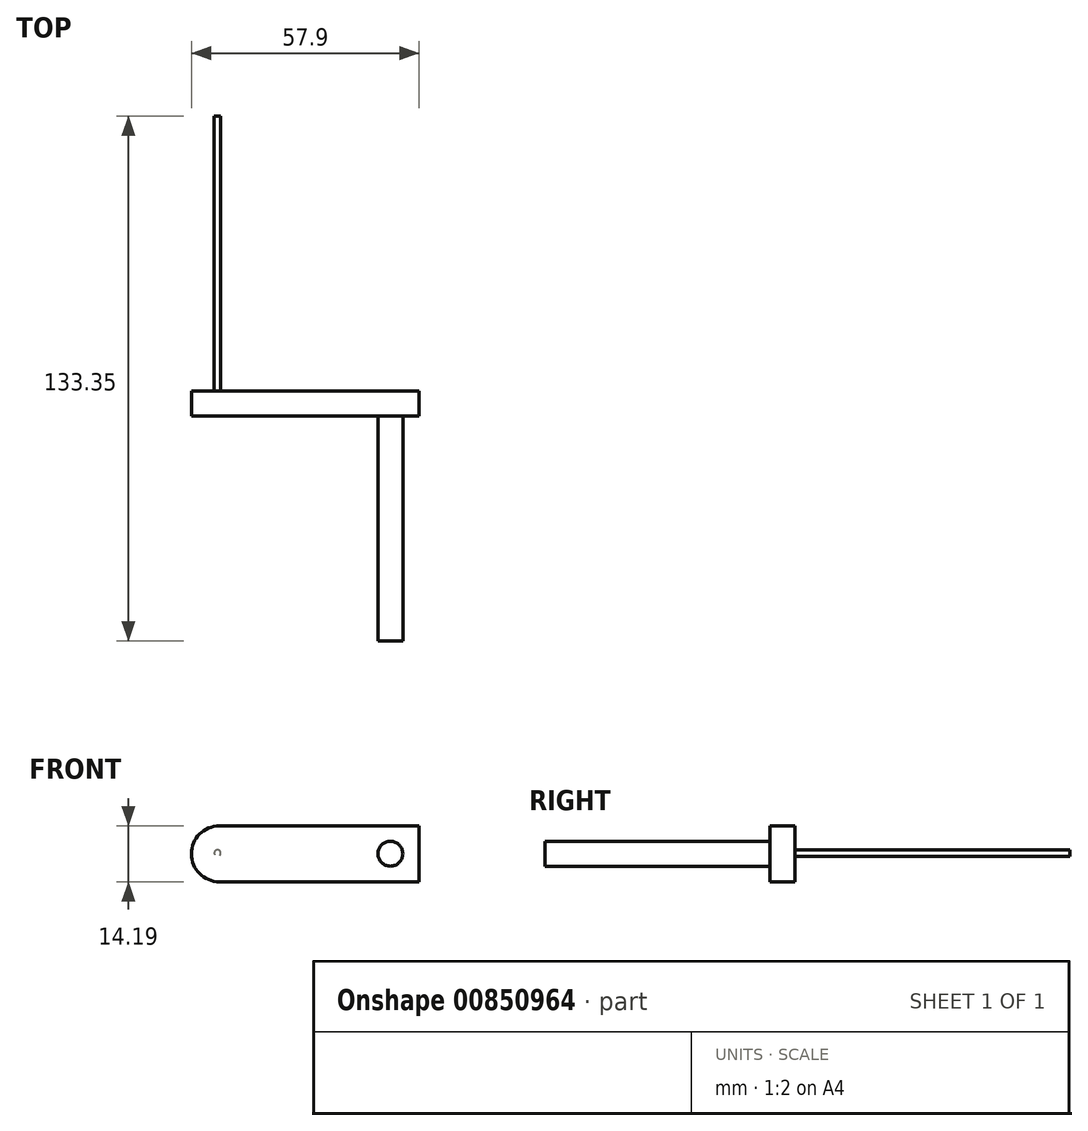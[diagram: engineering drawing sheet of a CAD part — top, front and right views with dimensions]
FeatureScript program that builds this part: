
annotation { "Feature Type Name" : "Feature", "Feature Type Description" : "" }
export const myFeature = defineFeature(function(context is Context, id is Id, definition is map)
    precondition{}
    {
        {
            var Q0;
            Q0=qCreatedBy(makeId("Front.planeOp"),FACE);
            var sketch = newSketch(context, id + "F0", { "sketchPlane" : qUnion([Q0])});
            skLineSegment(sketch, "E0.bottom", {"start": v(-42.12, 21.25) * mm, "end": v(8.68, 21.25) * mm});
            skLineSegment(sketch, "E0.top", {"start": v(-42.12, 7.06) * mm, "end": v(8.68, 7.06) * mm});
            skLineSegment(sketch, "E0.right", {"start": v(8.68, 21.25) * mm, "end": v(8.68, 7.06) * mm});
            skArc(sketch, "E1", {"start": v(-42.12, 21.25) * mm, "mid": v(-49.22, 14.15) * mm, "end": v(-42.12, 7.06) * mm});
            skPoint(sketch, "E2", {"position": v(-42.12, 21.25) * mm});
            skPoint(sketch, "E3", {"position": v(-42.12, 7.06) * mm});
            skSolve(sketch);
        }
        {
            var Q0;
            Q0=makeQuery(id+"F0.imprint","IMPRINT",FACE,{"disambiguationData":[TD([[makeQuery(id+"F0.imprint","IMPRINT",EDGE,{"derivedFrom":sQuery(id+"F0.wireOp",EDGE,"E0.bottom")}),-1.0]])]});
            extrude(context, id + "F1", {"entities" : qUnion([Q0]), "depth" : 6.35 * mm, "offsetDistance" : 25.4 * mm});
        }
        {
            var Q0;
            Q0=makeQuery(id+"F1.opExtrude","CAP_FACE",FACE,{"disambiguationData":[OSD([sQuery(id+"F0.wireOp",EDGE,"E0.bottom"),sQuery(id+"F0.wireOp",EDGE,"E0.top"),sQuery(id+"F0.wireOp",EDGE,"E0.right"),sQuery(id+"F0.wireOp",EDGE,"E1"),sQuery(id+"F0.wireOp",EDGE,"cYWnUQRV-fGSr-Q5LM-tKaJ-2oR27xkRg5be")])],"isStart":false});
            var sketch = newSketch(context, id + "F2", { "sketchPlane" : qUnion([Q0])});
            skSolve(sketch);
        }
        {
            var Q0;
            Q0=makeQuery(id+"F2.imprint","IMPRINT",FACE,{"disambiguationData":[TD([[makeQuery(id+"F2.imprint","IMPRINT",EDGE,{"derivedFrom":makeQuery(id+"F1.opExtrude","CAP_EDGE",EDGE,{"disambiguationData":[OSD([sQuery(id+"F0.wireOp",EDGE,"E0.bottom")])],"isStart":false})}),-1.0]])]});
            var sketch = newSketch(context, id + "F3", { "sketchPlane" : qUnion([Q0])});
            skSolve(sketch);
        }
        {
            var Q0;
            Q0=makeQuery(id+"F3.imprint","IMPRINT",FACE,{"disambiguationData":[TD([[makeQuery(id+"F3.imprint","IMPRINT",EDGE,{"derivedFrom":makeQuery(id+"F2.imprint","IMPRINT",EDGE,{"derivedFrom":makeQuery(id+"F1.opExtrude","CAP_EDGE",EDGE,{"disambiguationData":[OSD([sQuery(id+"F0.wireOp",EDGE,"E0.bottom")])],"isStart":false})})}),-1.0]])]});
            var sketch = newSketch(context, id + "F4", { "sketchPlane" : qUnion([Q0])});
            skCircle(sketch, "E4", {"center": v(1.34, 14.2) * mm, "radius": 3.17 * mm});
            skSolve(sketch);
        }
        {
            var Q0;
            Q0=makeQuery(id+"F3.imprint","IMPRINT",FACE,{"disambiguationData":[TD([[makeQuery(id+"F3.imprint","IMPRINT",EDGE,{"derivedFrom":makeQuery(id+"F2.imprint","IMPRINT",EDGE,{"derivedFrom":makeQuery(id+"F1.opExtrude","CAP_EDGE",EDGE,{"disambiguationData":[OSD([sQuery(id+"F0.wireOp",EDGE,"E0.bottom")])],"isStart":false})})}),-1.0]])]});
            var sketch = newSketch(context, id + "F5", { "sketchPlane" : qUnion([Q0])});
            skCircle(sketch, "E5", {"center": v(-42.58, 14.33) * mm, "radius": 0.83 * mm});
            skSolve(sketch);
        }
        {
            var Q0;
            Q0=makeQuery(id+"F5.imprint","IMPRINT",FACE,{"disambiguationData":[TD([[makeQuery(id+"F5.imprint","IMPRINT",EDGE,{"derivedFrom":sQuery(id+"F5.wireOp",EDGE,"E5")}),1.0]])]});
            extrude(context, id + "F6", {"entities" : qUnion([Q0]), "operationType" : NewBodyOperationType.ADD, "oppositeDirection" : true, "depth" : 76.2 * mm, "offsetDistance" : 25.4 * mm});
        }
        {
            var Q0;
            Q0=makeQuery(id+"F4.imprint","IMPRINT",FACE,{"disambiguationData":[TD([[makeQuery(id+"F4.imprint","IMPRINT",EDGE,{"derivedFrom":sQuery(id+"F4.wireOp",EDGE,"E4")}),1.0]])]});
            extrude(context, id + "F7", {"entities" : qUnion([Q0]), "operationType" : NewBodyOperationType.ADD, "depth" : 57.15 * mm, "offsetDistance" : 25.4 * mm});
        }
    });
